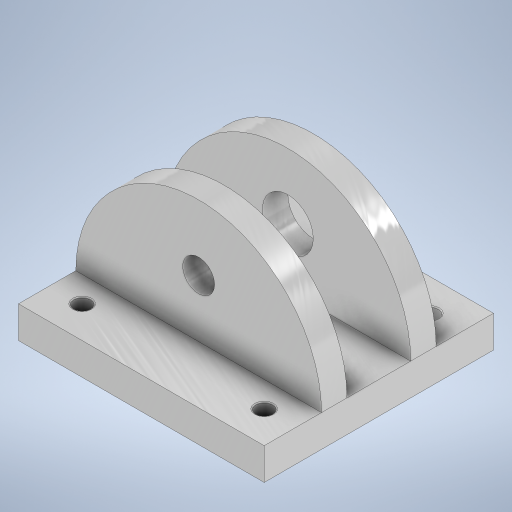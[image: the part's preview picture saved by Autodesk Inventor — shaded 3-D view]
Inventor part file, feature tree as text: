
AUTODESK INVENTOR PART (.ipt)
format: ipt  version: 2023 (Build 270158000, 158)  size: 337,920 bytes
history: native  units: in
note: dims shown in document units (in); Inventor stores cm internally (conversion verified against a paired STEP export)
features: sketch x6, extrude x4, plane x2, hole x1, fillet x1, mirror x1
ambient origin geometry x8: Origin, YZ Plane, XZ Plane, XY Plane, X Axis, Y Axis, Z Axis, Center Point
bodies: Solid1 (feature_tree)
feature tree (15):
  extrude  "Extrusion1"  Depth=1.8in
  sketch  "Sketch3"  dims[d2=0.25in d3=0.0in d4=0.5in d5=0.65in]
  hole  "Hole1"  [1 undecoded]
  fillet  "Fillet1"  Radius=0.65in
  plane  "Work Plane1"
  extrude  "Extrusion2"  Depth=0.25in
  plane  "Work Plane2"
  mirror  "Mirror1"
  extrude  "Extrusion3"  Depth=0.25in
  extrude  "Extrusion5"  Depth=0.25in
  sketch  "Sketch1"  dims[d0=1.929in d1=1.8in]
  sketch  "Sketch4"  dims[d6=0.242in d7=0.25in]
  sketch  "Sketch5"  dims[d8=0.25in d9=0.25in]
  sketch  "Sketch6"  dims[d10=0.25in d11=0.25in]
  sketch  "Sketch8"  dims[d12=0.25in d13=0.25in d14=0.25in d15=0.1339in d16=0.75in d17=0.256in d18=0.118in d19=90.0deg d20=0.3937in d21=0.8108in d22=0.0079in d23=-0.65in d24=0.2in d25=0.0in d26=-0.9in d27=0.45in d28=0.25in d29=1.0in d30=0.0in d34=0.4in d35=1.0in d36=0.0in]
note: 1 required parameter value undecoded (feature->parameter linkage not recoverable at this tier; creation-order binding heuristic only, values carry confidence <= 0.55)
